# Revit family: Ecowool Partition Wall BAtts (18kgm3)
name_source: partatom
category: Generic Models
units: mm (PartAtom-declared; Revit-internal decimal feet)

## family parameters
Can host rebar = No
Cut with Voids When Loaded = No
Host = Face
Part Type = Normal
Room Calculation Point = No
Round Connector Dimension = Use Diameter
Shared = No

## types (1)
- R0.7 - 25mm
    Default Elevation = 1219 mm
    Density = 18.00 kg/m³
    Description = ECOWOOL Brownie blanket and slabs are resilient, non-combustible, glass mineral wool products, supplied at roofing and walling application for residential and commercial building
    Finish = Partition Wall Batts
    Insulation Thickness = 25 mm  [stored 0.082021 ft]
    Manufacturer = PGF Insulation Sdn. Bhd.
    Thermal K value = 0.0366
    Thermal R value = 0.7
    Type of Insulation = Glass Mineral Wool Blanket
    URL = www.ecowool.com.my

note: [stored X ft] marks values corroborated as IEEE doubles in the binary element streams (Revit-internal decimal feet)

## geometry (parser evidence)
native form markers: Sweep x2
no freeform markers — native parametric forms only
